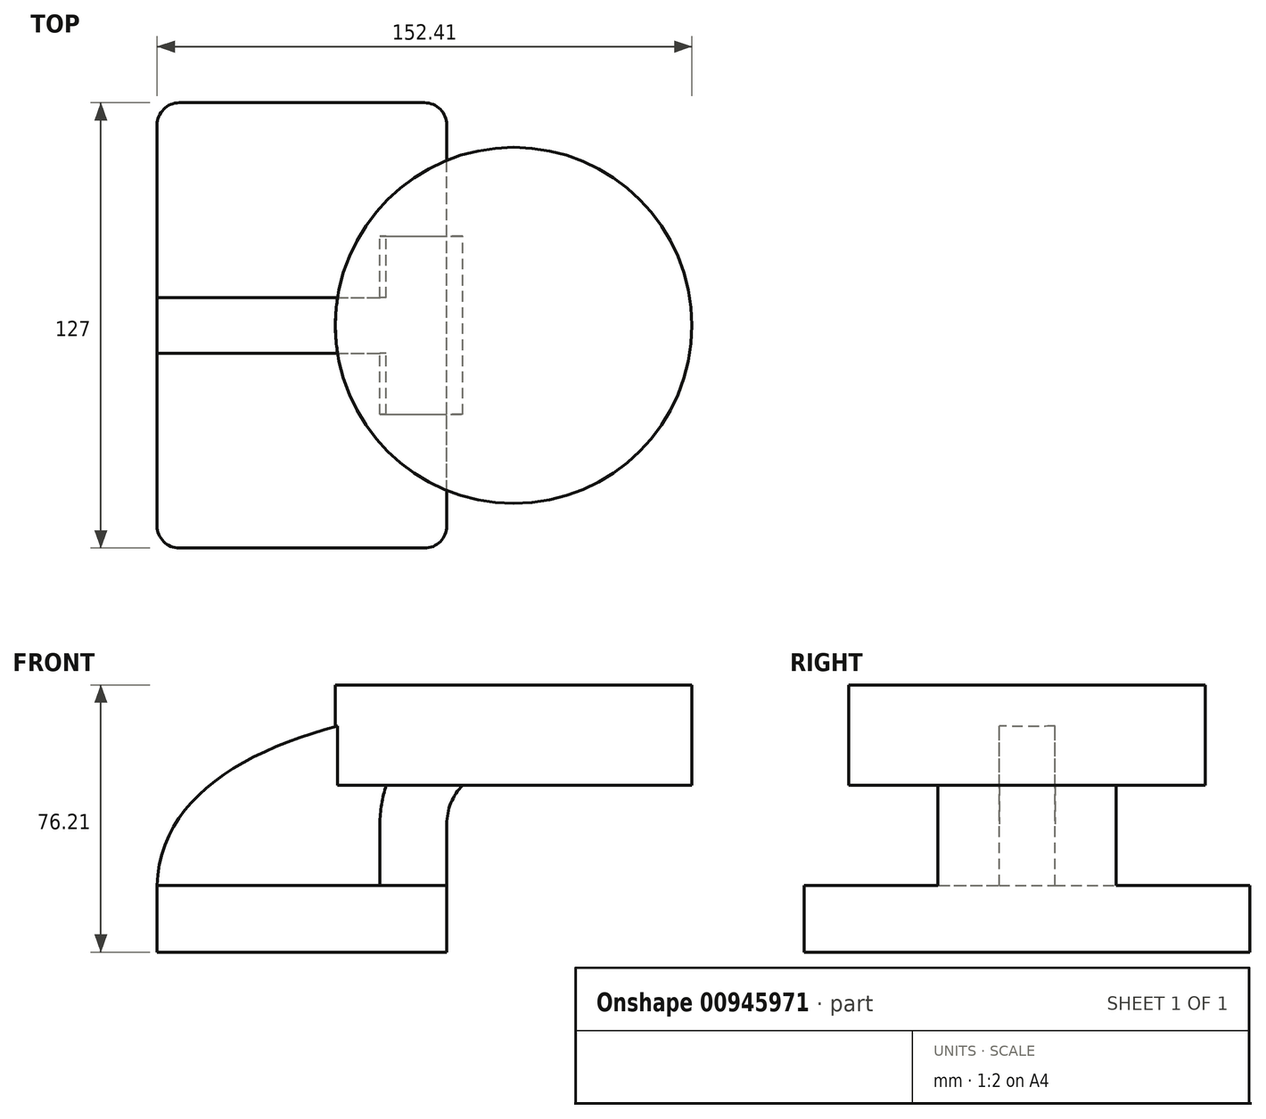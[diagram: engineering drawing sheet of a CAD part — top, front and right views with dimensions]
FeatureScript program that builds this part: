
annotation { "Feature Type Name" : "Feature", "Feature Type Description" : "" }
export const myFeature = defineFeature(function(context is Context, id is Id, definition is map)
    precondition{}
    {
        {
            var Q0;
            Q0=qCreatedBy(makeId("Front.planeOp"),FACE);
            var sketch = newSketch(context, id + "F0", { "sketchPlane" : qUnion([Q0])});
            skLineSegment(sketch, "E0.bottom", {"start": v(-41.28, 9.52) * mm, "end": v(41.28, 9.53) * mm});
            skLineSegment(sketch, "E0.top", {"start": v(-41.28, -9.53) * mm, "end": v(41.28, -9.53) * mm});
            skLineSegment(sketch, "E0.left", {"start": v(-41.28, 9.52) * mm, "end": v(-41.28, -9.53) * mm});
            skLineSegment(sketch, "E0.right", {"start": v(41.28, 9.53) * mm, "end": v(41.28, -9.52) * mm});
            skPoint(sketch, "E0.middle", {"position": v(0, 0) * mm});
            skLineSegment(sketch, "E1.bottom", {"start": v(111.12, 66.68) * mm, "end": v(60.32, 66.68) * mm});
            skLineSegment(sketch, "E1.top", {"start": v(111.12, 38.1) * mm, "end": v(60.33, 38.1) * mm});
            skLineSegment(sketch, "E1.left", {"start": v(111.12, 66.68) * mm, "end": v(111.12, 38.1) * mm});
            skLineSegment(sketch, "E1.right", {"start": v(60.32, 66.68) * mm, "end": v(60.33, 38.1) * mm});
            skPoint(sketch, "E1.middle", {"position": v(85.72, 52.39) * mm});
            skLineSegment(sketch, "E2", {"start": v(41.27, 9.53) * mm, "end": v(41.27, 27) * mm});
            skArc(sketch, "E3", {"start": v(41.27, 27) * mm, "mid": v(45.92, 38.23) * mm, "end": v(57.15, 42.88) * mm});
            skLineSegment(sketch, "E4", {"start": v(57.15, 42.88) * mm, "end": v(85.72, 42.88) * mm});
            skLineSegment(sketch, "E5.0", {"start": v(57.15, 61.93) * mm, "end": v(85.72, 61.93) * mm});
            skArc(sketch, "E5.1", {"start": v(22.23, 27) * mm, "mid": v(32.45, 51.7) * mm, "end": v(57.15, 61.93) * mm});
            skLineSegment(sketch, "E5.2", {"start": v(22.22, 9.53) * mm, "end": v(22.22, 27) * mm});
            skFitSpline(sketch, "E6", {"points": [v(-41.28, 9.52) * mm, v(57.15, 61.93) * mm], "startDerivative": vector(3.12, 107.76) * mm, "endDerivative": vector(140.93, 7.65) * mm});
            skSolve(sketch);
        }
        {
            var Q0;
            Q0=makeQuery(id+"F0.imprint","IMPRINT",FACE,{"disambiguationData":[TD([[makeQuery(id+"F0.imprint","IMPRINT",EDGE,{"derivedFrom":sQuery(id+"F0.wireOp",EDGE,"E0.top")}),1.0]])]});
            extrude(context, id + "F1", {"entities" : qUnion([Q0]), "endBound" : BoundingType.SYMMETRIC, "depth" : 127 * mm, "offsetDistance" : 25.4 * mm});
        }
        {
            var Q0;
            {var subQ1=sQuery(id+"F0.wireOp",EDGE,"E2");Q0=makeQuery(id+"F0.imprint","IMPRINT",FACE,{"disambiguationData":[TD([[makeQuery(id+"F0.imprint","IMPRINT",EDGE,{"derivedFrom":subQ1}),1.0]])]});}
            extrude(context, id + "F2", {"entities" : qUnion([Q0]), "operationType" : NewBodyOperationType.ADD, "endBound" : BoundingType.SYMMETRIC, "depth" : 50.8 * mm, "offsetDistance" : 25.4 * mm});
        }
        {
            var Q0;
            {var subQ3=sQuery(id+"F0.wireOp",EDGE,"E5.2");Q0=makeQuery(id+"F0.imprint","IMPRINT",FACE,{"disambiguationData":[TD([[makeQuery(id+"F0.imprint","IMPRINT",EDGE,{"derivedFrom":subQ3}),1.0]])]});}
            extrude(context, id + "F3", {"entities" : qUnion([Q0]), "operationType" : NewBodyOperationType.ADD, "endBound" : BoundingType.SYMMETRIC, "depth" : 15.88 * mm, "offsetDistance" : 25.4 * mm});
        }
        {
            var Q0;
            {var subQ1=sQuery(id+"F0.wireOp",EDGE,"E1.bottom");Q0=makeQuery(id+"F0.imprint","IMPRINT",FACE,{"disambiguationData":[TD([[makeQuery(id+"F0.imprint","IMPRINT",EDGE,{"derivedFrom":subQ1}),1.0]])]});}
            var Q1;
            Q1=sQuery(id+"F0.wireOp",EDGE,"E1.right");
            revolve(context, id + "F4", {"operationType" : NewBodyOperationType.ADD, "surfaceOperationType" : NewSurfaceOperationType.NEW, "entities" : qUnion([Q0]), "axis" : qUnion([Q1]), "revolveType" : RevolveType.FULL});
        }
        {
            var Q0;
            Q0=makeQuery(id+"F1.opExtrude","CAP_EDGE",EDGE,{"disambiguationData":[OSD([sQuery(id+"F0.wireOp",EDGE,"E0.left")])],"isStart":false});
            var Q1;
            Q1=makeQuery(id+"F1.opExtrude","CAP_EDGE",EDGE,{"disambiguationData":[OSD([sQuery(id+"F0.wireOp",EDGE,"E0.right")])],"isStart":false});
            var Q2;
            Q2=makeQuery(id+"F1.opExtrude","CAP_EDGE",EDGE,{"disambiguationData":[OSD([sQuery(id+"F0.wireOp",EDGE,"E0.right")])],"isStart":true});
            var Q3;
            Q3=makeQuery(id+"F1.opExtrude","CAP_EDGE",EDGE,{"disambiguationData":[OSD([sQuery(id+"F0.wireOp",EDGE,"E0.left")])],"isStart":true});
            fillet(context, id + "F5", {"entities" : qUnion([Q0, Q1, Q2, Q3]), "radius" : 6.35 * mm, "tangentPropagation" : true, "allowEdgeOverflow" : false});
        }
    });
